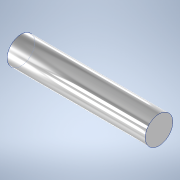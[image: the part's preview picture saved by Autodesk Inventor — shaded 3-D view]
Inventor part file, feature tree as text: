
AUTODESK INVENTOR PART (.ipt)
format: ipt  version: 2020.3 (Build 243373000, 373)  size: 98,304 bytes
history: native  units: mm
features: other x1, extrude x1, sketch x1
ambient origin geometry x8: Origin, YZ Plane, XZ Plane, XY Plane, X Axis, Y Axis, Z Axis, Center Point
bodies: Body1 (feature_tree)
feature tree (3):
  other  "ソリッド1"
  extrude  "押し出し1"  Depth=6.0mm
  sketch  "スケッチ1"
